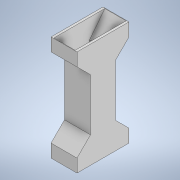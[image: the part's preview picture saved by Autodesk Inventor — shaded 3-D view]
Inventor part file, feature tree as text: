
AUTODESK INVENTOR PART (.ipt)
format: ipt  version: 2022 (Build 260153000, 153)  size: 181,248 bytes
history: native  units: mm
features: extrude x7, sketch x7, plane x2, mirror x1
ambient origin geometry x8: Origin, YZ Plane, XZ Plane, XY Plane, X Axis, Y Axis, Z Axis, Center Point
bodies: Solid1 (feature_tree)
feature tree (17):
  extrude  "Extrusion1"  Depth=80.0mm
  plane  "Work Plane1"
  extrude  "Extrusion2"  Depth=12.7mm
  extrude  "Extrusion3"  Depth=3.0mm
  extrude  "Extrusion4"  Depth=3.0mm
  extrude  "Extrusion5"  Depth=32.8mm TaperAngle=0.0deg
  extrude  "Extrusion6"  Depth=3.0mm TaperAngle=0.0deg
  extrude  "Extrusion7"  Depth=3.6mm
  plane  "Work Plane2"
  mirror  "Mirror1"
  sketch  "Sketch1"  dims[d0=34.0mm d1=80.0mm]
  sketch  "Sketch2"  dims[d2=30.0mm d3=0.0mm d4=12.7mm]
  sketch  "Sketch3"  dims[d5=12.7mm d6=3.0mm]
  sketch  "Sketch4"  dims[d7=0.75mm d8=3.0mm]
  sketch  "Sketch5"  dims[d9=0.75mm d10=32.8mm d11=0.0mm]
  sketch  "Sketch6"  dims[d12=3.0mm d13=0.0mm d14=3.0mm d15=0.0mm]
  sketch  "Sketch7"  dims[d16=10.0mm d17=10.0mm d18=10.0mm d19=0.0mm d20=0.0mm d21=3.6mm d22=76.2mm d23=0.0mm d24=45.0deg d25=0.0mm d26=0.0mm d27=-25.4mm]
